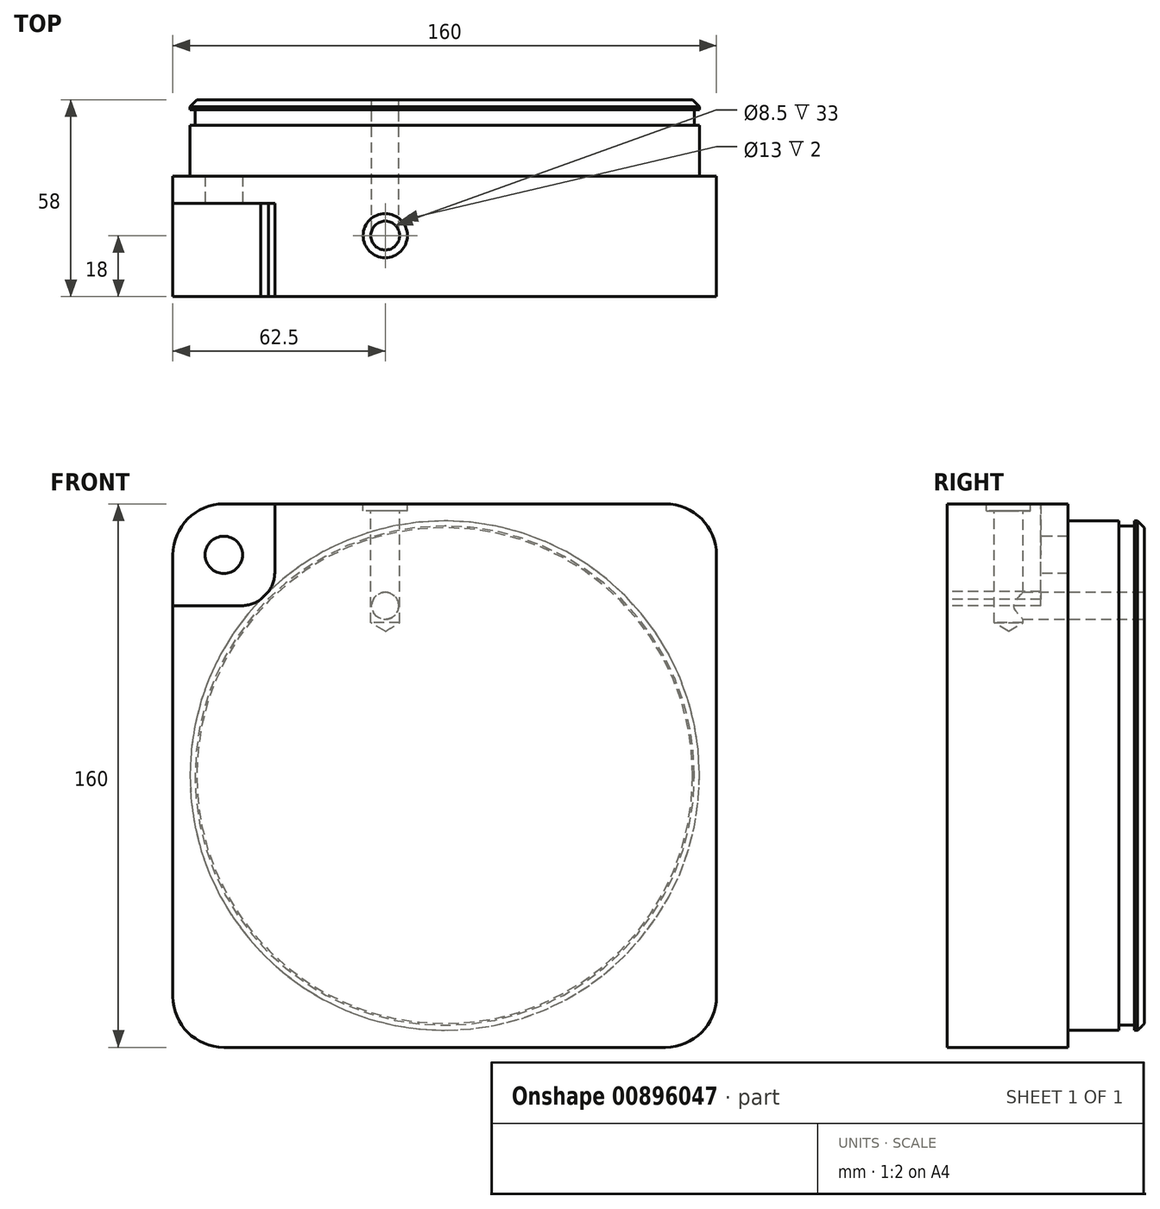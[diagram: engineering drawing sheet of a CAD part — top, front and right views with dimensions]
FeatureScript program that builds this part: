
annotation { "Feature Type Name" : "Feature", "Feature Type Description" : "" }
export const myFeature = defineFeature(function(context is Context, id is Id, definition is map)
    precondition{}
    {
        {
            var Q0;
            Q0=qCreatedBy(makeId("Front.planeOp"),FACE);
            var sketch = newSketch(context, id + "F0", { "sketchPlane" : qUnion([Q0])});
            skLineSegment(sketch, "E0.bottom", {"start": v(65, -80) * mm, "end": v(-65, -80) * mm});
            skLineSegment(sketch, "E0.top", {"start": v(65, 80) * mm, "end": v(-65, 80) * mm});
            skLineSegment(sketch, "E0.left", {"start": v(80, -65) * mm, "end": v(80, 65) * mm});
            skLineSegment(sketch, "E0.right", {"start": v(-80, -65) * mm, "end": v(-80, 65) * mm});
            skPoint(sketch, "E0.middle", {"position": v(0, 0) * mm});
            skPoint(sketch, "E1.visualSharp", {"position": v(-80, 80) * mm});
            skArc(sketch, "E1.filletArc", {"start": v(-65, 80) * mm, "mid": v(-75.6, 75.6) * mm, "end": v(-80, 65) * mm});
            skPoint(sketch, "E2.visualSharp", {"position": v(80, 80) * mm});
            skArc(sketch, "E2.filletArc", {"start": v(80, 65) * mm, "mid": v(75.6, 75.6) * mm, "end": v(65, 80) * mm});
            skPoint(sketch, "E3.visualSharp", {"position": v(80, -80) * mm});
            skArc(sketch, "E3.filletArc", {"start": v(65, -80) * mm, "mid": v(75.6, -75.6) * mm, "end": v(80, -65) * mm});
            skPoint(sketch, "E4.visualSharp", {"position": v(-80, -80) * mm});
            skArc(sketch, "E4.filletArc", {"start": v(-80, -65) * mm, "mid": v(-75.6, -75.6) * mm, "end": v(-65, -80) * mm});
            skLineSegment(sketch, "E5", {"start": v(-80, 50) * mm, "end": v(-60, 50) * mm});
            skLineSegment(sketch, "E6", {"start": v(-50, 60) * mm, "end": v(-50, 80) * mm});
            skPoint(sketch, "E7.visualSharp", {"position": v(-50, 50) * mm});
            skArc(sketch, "E7.filletArc", {"start": v(-60, 50) * mm, "mid": v(-52.93, 52.93) * mm, "end": v(-50, 60) * mm});
            skCircle(sketch, "E8", {"center": v(-65, 65) * mm, "radius": 5.5 * mm});
            skCircle(sketch, "E9", {"center": v(0, 0) * mm, "radius": 75 * mm});
            skSolve(sketch);
        }
        {
            var Q0;
            {var subQ0=sQuery(id+"F0.wireOp",EDGE,"E9");var subQ1=sQuery(id+"F0.wireOp",EDGE,"E7.filletArc");var subQ2=makeQuery(id+"F0.imprint","INTERSECT",VERTEX,{"disambiguationData":[OD(0.0)],"derivedFrom":[subQ1,subQ0]});Q0=makeQuery(id+"F0.imprint","IMPRINT",FACE,{"disambiguationData":[TD([[makeQuery(id+"F0.imprint","IMPRINT",EDGE,{"disambiguationData":[TD([[subQ2,-1.0]])],"derivedFrom":subQ1}),-1.0]])]});}
            var Q1;
            {var subQ0=sQuery(id+"F0.wireOp",EDGE,"E9");var subQ1=sQuery(id+"F0.wireOp",EDGE,"E7.filletArc");var subQ2=makeQuery(id+"F0.imprint","INTERSECT",VERTEX,{"disambiguationData":[OD(0.0)],"derivedFrom":[subQ1,subQ0]});Q1=makeQuery(id+"F0.imprint","IMPRINT",FACE,{"disambiguationData":[TD([[makeQuery(id+"F0.imprint","IMPRINT",EDGE,{"disambiguationData":[TD([[subQ2,-1.0]])],"derivedFrom":subQ1}),1.0]])]});}
            extrude(context, id + "F1", {"entities" : qUnion([Q0, Q1]), "oppositeDirection" : true, "depth" : 58 * mm, "offsetDistance" : 25 * mm});
        }
        {
            var Q0;
            Q0 = qSketchRegion(id + "F0", true);
            var Q1;
            Q1=makeQuery(id+"F0.imprint","IMPRINT",FACE,{"disambiguationData":[TD([[makeQuery(id+"F0.imprint","IMPRINT",EDGE,{"derivedFrom":sQuery(id+"F0.wireOp",EDGE,"E8")}),1.0]])]});
            extrude(context, id + "F2", {"entities" : qUnion([Q0, Q1]), "operationType" : NewBodyOperationType.ADD, "oppositeDirection" : true, "depth" : (58 - 22.5) * mm, "offsetDistance" : 25 * mm});
        }
        {
            var Q0;
            Q0=makeQuery(id+"F0.imprint","IMPRINT",FACE,{"disambiguationData":[TD([[makeQuery(id+"F0.imprint","IMPRINT",EDGE,{"derivedFrom":sQuery(id+"F0.wireOp",EDGE,"E8")}),1.0]])]});
            var Q1;
            Q1=makeQuery(id+"F2.opExtrude","CAP_FACE",FACE,{"disambiguationData":[OSD([sQuery(id+"F0.wireOp",EDGE,"E0.bottom"),sQuery(id+"F0.wireOp",EDGE,"E0.top"),sQuery(id+"F0.wireOp",EDGE,"E0.left"),sQuery(id+"F0.wireOp",EDGE,"E0.right"),sQuery(id+"F0.wireOp",EDGE,"E1.filletArc"),sQuery(id+"F0.wireOp",EDGE,"E2.filletArc"),sQuery(id+"F0.wireOp",EDGE,"E3.filletArc"),sQuery(id+"F0.wireOp",EDGE,"E4.filletArc"),sQuery(id+"F0.wireOp",EDGE,"E9")])],"isStart":false});
            extrude(context, id + "F3", {"entities" : qUnion([Q0]), "operationType" : NewBodyOperationType.REMOVE, "endBound" : BoundingType.UP_TO_SURFACE, "oppositeDirection" : true, "depth" : 25 * mm, "endBoundEntityFace" : qUnion([Q1]), "offsetDistance" : 25 * mm});
        }
        {
            var Q0;
            {var subQ0=sQuery(id+"F0.wireOp",EDGE,"E1.filletArc");Q0=makeQuery(id+"F0.imprint","IMPRINT",FACE,{"disambiguationData":[TD([[makeQuery(id+"F0.imprint","IMPRINT",EDGE,{"derivedFrom":subQ0}),1.0]])]});}
            extrude(context, id + "F4", {"entities" : qUnion([Q0]), "operationType" : NewBodyOperationType.REMOVE, "oppositeDirection" : true, "depth" : (35.5 - 8) * mm, "offsetDistance" : 25 * mm});
        }
        {
            var Q0;
            Q0=makeQuery(id+"F1.opExtrude","CAP_EDGE",EDGE,{"disambiguationData":[OSD([sQuery(id+"F0.wireOp",EDGE,"E9")])],"isStart":false});
            chamfer(context, id + "F5", {"entities" : qUnion([Q0]), "width" : 2 * mm, "tangentPropagation" : true});
        }
        {
            var Q0;
            Q0=makeQuery(id+"F2.opExtrude","SWEPT_FACE",FACE,{"disambiguationData":[OSD([sQuery(id+"F0.wireOp",EDGE,"E0.top")])]});
            var sketch = newSketch(context, id + "F6", { "sketchPlane" : qUnion([Q0])});
            skPoint(sketch, "E10", {"position": v(-17.5, 18) * mm});
            skSolve(sketch);
        }
        {
            var Q0;
            Q0=sQuery(id+"F6.wireOp",VERTEX,"E10");
            var Q1;
            Q1=makeQuery(id+"F1.opExtrude","SWEPT_BODY",BODY,{"disambiguationData":[OSD([sQuery(id+"F0.wireOp",EDGE,"E9")])]});
            hole(context, id + "F7", {"style" : HoleStyle.C_BORE, "endStyle" : HoleEndStyle.BLIND, "holeDiameter" : 8.5 * mm, "cBoreDiameter" : 13 * mm, "cBoreDepth" : 2 * mm, "majorDiameter" : 10 * mm, "holeDepth" : 35 * mm, "isTappedThrough" : true, "tappedDepth" : 20 * mm, "tapClearance" : 3, "startFromSketch" : true, "locations" : qUnion([Q0]), "scope" : qUnion([Q1])});
        }
        {
            var Q0;
            Q0=makeQuery(id+"F1.opExtrude","CAP_FACE",FACE,{"disambiguationData":[OSD([sQuery(id+"F0.wireOp",EDGE,"E9")])],"isStart":false});
            var sketch = newSketch(context, id + "F8", { "sketchPlane" : qUnion([Q0])});
            skPoint(sketch, "E11.0", {"position": v(17.5, 80) * mm});
            skLineSegment(sketch, "E12", {"start": v(17.5, 80) * mm, "end": v(17.5, 50) * mm, "construction": true});
            skSolve(sketch);
        }
        {
            var Q0;
            Q0=sQuery(id+"F8.wireOp",VERTEX,"E12.end");
            var Q1;
            Q1=makeQuery(id+"F1.opExtrude","SWEPT_BODY",BODY,{"disambiguationData":[OSD([sQuery(id+"F0.wireOp",EDGE,"E9")])]});
            hole(context, id + "F9", {"style" : HoleStyle.SIMPLE, "endStyle" : HoleEndStyle.BLIND, "holeDiameter" : 8 * mm, "majorDiameter" : 5 * mm, "holeDepth" : 40 * mm, "isTappedThrough" : true, "tappedDepth" : 20 * mm, "tapClearance" : 3, "startFromSketch" : true, "locations" : qUnion([Q0]), "scope" : qUnion([Q1])});
        }
        {
            var Q0;
            Q0=qCreatedBy(makeId("Right.planeOp"),FACE);
            var sketch = newSketch(context, id + "F10", { "sketchPlane" : qUnion([Q0])});
            skLineSegment(sketch, "E13.bottom", {"start": v(55, 75) * mm, "end": v(50.5, 75) * mm});
            skLineSegment(sketch, "E13.top", {"start": v(55, 73.5) * mm, "end": v(50.5, 73.5) * mm});
            skLineSegment(sketch, "E13.left", {"start": v(55, 75) * mm, "end": v(55, 73.5) * mm});
            skLineSegment(sketch, "E13.right", {"start": v(50.5, 75) * mm, "end": v(50.5, 73.5) * mm});
            skLineSegment(sketch, "E14", {"start": v(0, 0) * mm, "end": v(58, 0) * mm, "construction": true});
            skSolve(sketch);
        }
        {
            var Q0;
            Q0 = qSketchRegion(id + "F10", true);
            var Q1;
            Q1=sQuery(id+"F10.wireOp",EDGE,"E14");
            revolve(context, id + "F11", {"operationType" : NewBodyOperationType.REMOVE, "surfaceOperationType" : NewSurfaceOperationType.NEW, "entities" : qUnion([Q0]), "axis" : qUnion([Q1]), "revolveType" : RevolveType.FULL, "oppositeDirection" : true});
        }
    });
